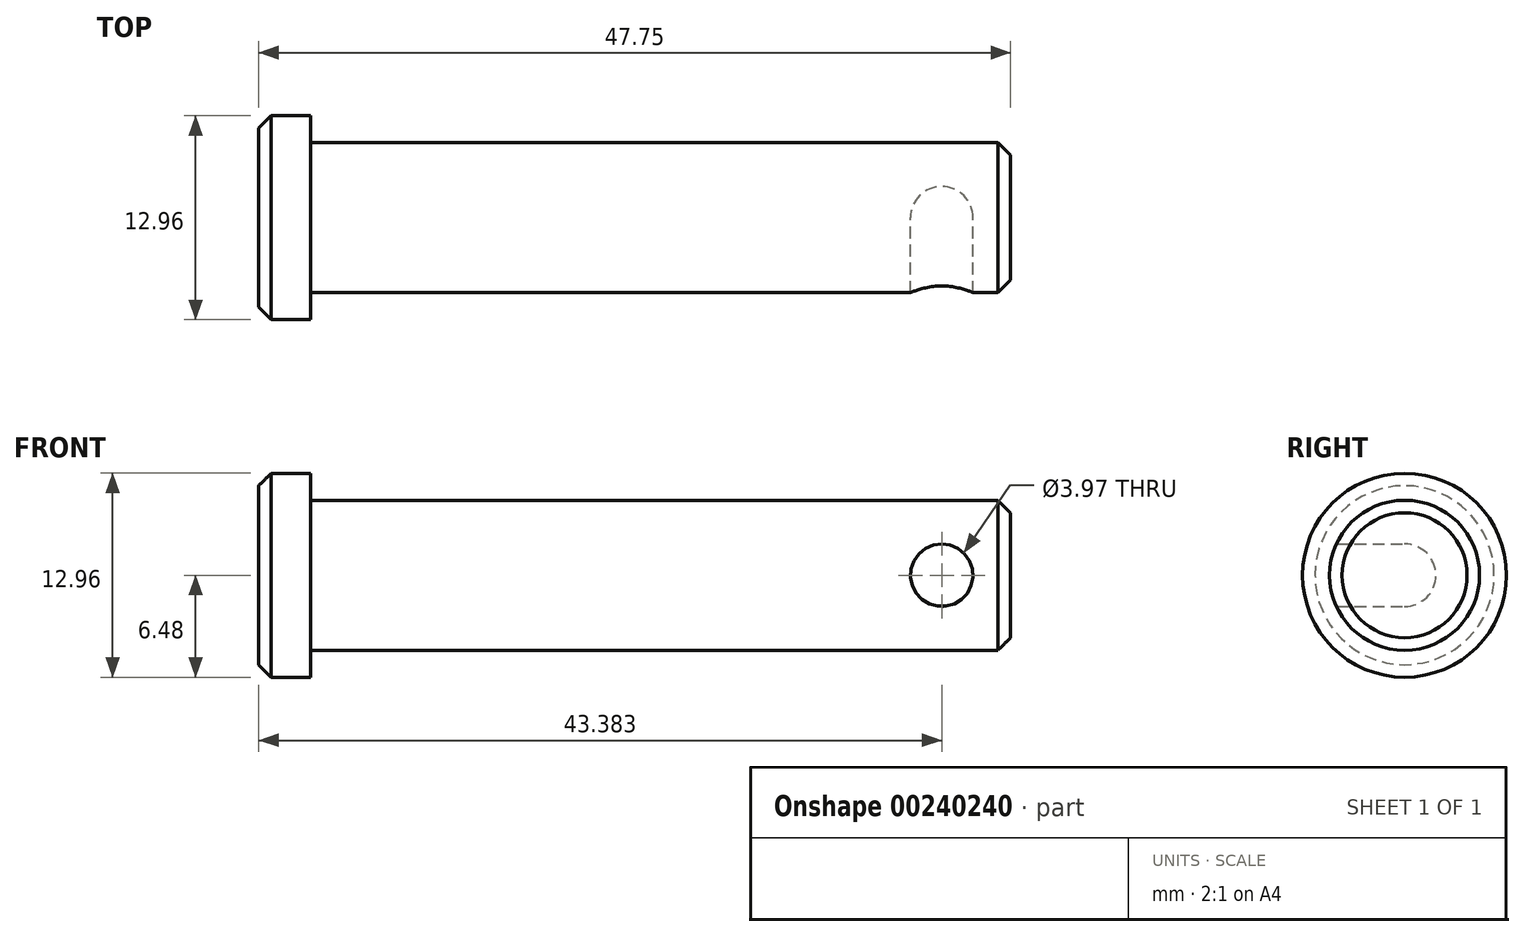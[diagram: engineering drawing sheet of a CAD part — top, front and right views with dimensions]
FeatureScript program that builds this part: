
annotation { "Feature Type Name" : "Feature", "Feature Type Description" : "" }
export const myFeature = defineFeature(function(context is Context, id is Id, definition is map)
    precondition{}
    {
        {
            var Q0;
            Q0=qCreatedBy(makeId("Front.planeOp"),FACE);
            var sketch = newSketch(context, id + "F0", { "sketchPlane" : qUnion([Q0])});
            skLineSegment(sketch, "E0", {"start": v(0, 0) * mm, "end": v(30.47, 0) * mm, "construction": true});
            skLineSegment(sketch, "E1", {"start": v(0, 0) * mm, "end": v(0, 6.48) * mm});
            skLineSegment(sketch, "E2", {"start": v(0, 6.48) * mm, "end": v(3.3, 6.48) * mm});
            skLineSegment(sketch, "E3", {"start": v(3.3, 6.48) * mm, "end": v(3.3, 4.76) * mm});
            skLineSegment(sketch, "E4", {"start": v(3.3, 4.76) * mm, "end": v(47.75, 4.76) * mm});
            skLineSegment(sketch, "E5", {"start": v(47.75, 4.76) * mm, "end": v(47.75, 0) * mm});
            skLineSegment(sketch, "E6", {"start": v(0, 0) * mm, "end": v(47.75, 0) * mm});
            skCircle(sketch, "E7", {"center": v(43.38, 0) * mm, "radius": 1.98 * mm});
            skSolve(sketch);
        }
        {
            var Q0;
            Q0 = qSketchRegion(id + "F0", true);
            var Q1;
            Q1=sQuery(id+"F0.wireOp",EDGE,"E6");
            revolve(context, id + "F1", {"entities" : qUnion([Q0]), "axis" : qUnion([Q1]), "revolveType" : RevolveType.FULL});
        }
        {
            var Q0;
            Q0=sQuery(id+"F0.wireOp",VERTEX,"E7.center");
            var Q1;
            Q1=makeQuery(id+"F1.opRevolve","SWEPT_BODY",BODY,{"disambiguationData":[OSD([sQuery(id+"F0.wireOp",EDGE,"E1"),sQuery(id+"F0.wireOp",EDGE,"E2"),sQuery(id+"F0.wireOp",EDGE,"E3"),sQuery(id+"F0.wireOp",EDGE,"E4"),sQuery(id+"F0.wireOp",EDGE,"E5"),sQuery(id+"F0.wireOp",EDGE,"E6"),sQuery(id+"F0.wireOp",EDGE,"E7")])]});
            hole(context, id + "F2", {"style" : HoleStyle.SIMPLE, "endStyle" : HoleEndStyle.THROUGH, "oppositeDirection" : true, "holeDiameter" : 3.97 * mm, "tappedDepth" : 12.7 * mm, "tapClearance" : 3, "locations" : qUnion([Q0]), "scope" : qUnion([Q1])});
        }
        {
            var Q0;
            Q0=makeQuery(id+"F1.opRevolve","SWEPT_EDGE",EDGE,{"disambiguationData":[OSD([sQuery(id+"F0.wireOp",EDGE,"E4"),sQuery(id+"F0.wireOp",EDGE,"E5")])]});
            var Q1;
            Q1=makeQuery(id+"F1.opRevolve","SWEPT_EDGE",EDGE,{"disambiguationData":[OSD([sQuery(id+"F0.wireOp",EDGE,"E1"),sQuery(id+"F0.wireOp",EDGE,"E2")])]});
            chamfer(context, id + "F3", {"entities" : qUnion([Q0, Q1]), "width" : 0.8 * mm, "tangentPropagation" : true});
        }
    });
